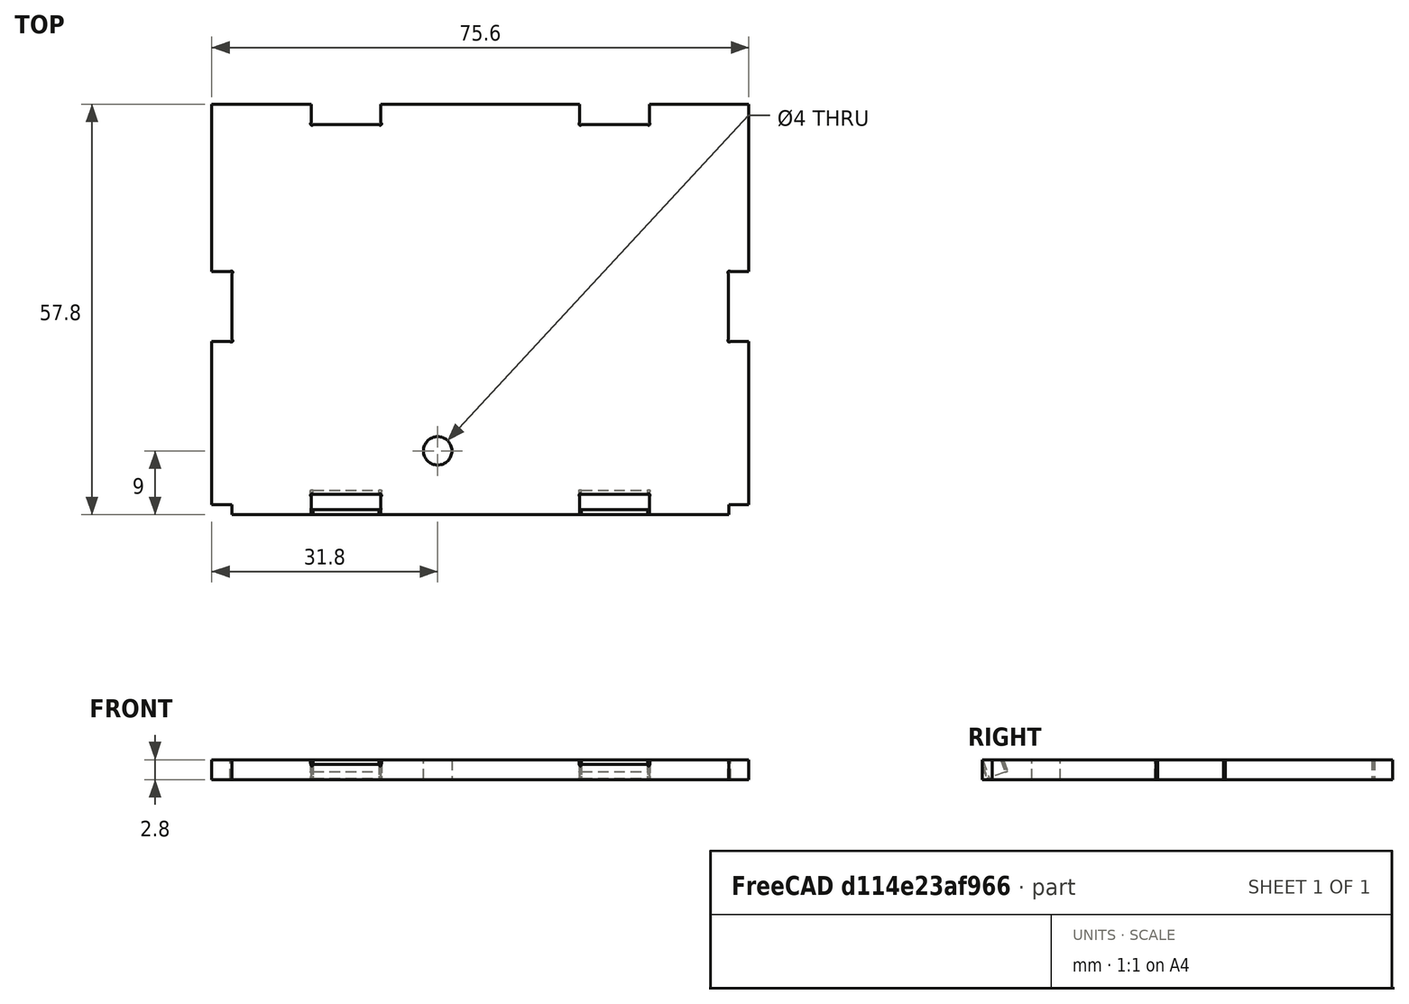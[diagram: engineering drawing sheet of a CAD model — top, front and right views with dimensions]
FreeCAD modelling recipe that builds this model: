
FCSTD DOCUMENT  (FreeCAD 1.0R39109 (Git))
Label: TheThing_v7_tabs_export
License: All rights reserved
LicenseURL: http://www.ohwr.org/attachments/2388/cern_ohl_v_1_2.txt
objects: Part::Feature×13, Part::Part2DObjectPython×12
note: 25 computed .brp shape members not serialized (recipe doc carries the construction recipe); baked Part::Feature solids carry a one-line shape summary decoded from their .brp

FEATURE [Part::Feature] test
  Placement = pos=(37.4,65.5,67.8) rot=(0,1,0;1.5708rad)
  shape: bbox 100.6 x 80.6 x 2.8 mm, 82 faces (baked)
FEATURE [Part::Feature] test001
  Placement = pos=(180.8,65.5,67.8) rot=(0,-1,0;1.5708rad)
  shape: bbox 100.6 x 80.6 x 2.8 mm, 70 faces (baked)
FEATURE [Part::Feature] test002
  Placement = pos=(187,118.5,93.2) rot=(0,-1,0;3.14159rad)
  shape: bbox 75.6 x 47.6 x 2.8 mm, 48 faces (baked)
FEATURE [Part::Feature] test003
  Placement = pos=(110,152.1,67.4) rot=(0,0,1;0rad)
  shape: bbox 75.6 x 77.8 x 2.8 mm, 42 faces (baked)
FEATURE [Part::Feature] test004
  Placement = pos=(109.4,62.1,33.2) rot=(0,-1,0;3.14159rad)
  shape: bbox 75.6 x 33.14 x 2.8 mm, 54 faces (baked)
FEATURE [Part::Feature] test005
  Placement = pos=(33,168.92,78.0359) rot=(-0.34202,0,0;2.79253rad)
  shape: bbox 75.6 x 17.92 x 2.8 mm, 18 faces (baked)
FEATURE [Part::Feature] test006
  Placement = pos=(33,156,12.7) rot=(1,0,0;1.5708rad)
  shape: bbox 75.6 x 104.4 x 2.8 mm, 110 faces (baked)
FEATURE [Part::Feature] test007
  Placement = pos=(110,209.68,-27.7) rot=(-1,0,0;1.5708rad)
  shape: bbox 75.6 x 44.36 x 2.8 mm, 108 faces (baked)
FEATURE [Part::Feature] test008
  Placement = pos=(187,149.16,4.32219) rot=(-0.939693,0,0;1.22173rad)
  shape: bbox 75.6 x 58.09 x 2.923 mm, 53 faces (baked)
FEATURE [Part::Feature] test009
  Placement = pos=(37.5,65.5,65.8) rot=(0,1,0;1.5708rad)
  shape: bbox 109.8 x 89.8 x 2.8 mm, 46 faces (baked)
FEATURE [Part::Feature] test010
  Placement = pos=(180.8,65.5,-3) rot=(0,1,0;4.71239rad)
  shape: bbox 109.8 x 89.8 x 2.8 mm, 46 faces (baked)
FEATURE [Part::Part2DObjectPython] Shape2DView  # Draft 2D object (typed FeaturePython)
  AutoUpdate = true
  Base = -> test
  Clip = false
  FuseArch = false
  HiddenLines = false
  InPlace = true
  OnlySolids = false
  Projection = (0,0,1)
  ProjectionMode = 0
  SegmentLength = 0.05
  Tessellation = false
  VisibleOnly = false
FEATURE [Part::Part2DObjectPython] Shape2DView001  # Draft 2D object (typed FeaturePython)
  AutoUpdate = true
  Base = -> test001
  Clip = false
  FuseArch = false
  HiddenLines = false
  InPlace = true
  OnlySolids = false
  Projection = (0,0,1)
  ProjectionMode = 0
  SegmentLength = 0.05
  Tessellation = false
  VisibleOnly = false
FEATURE [Part::Part2DObjectPython] Shape2DView002  # Draft 2D object (typed FeaturePython)
  AutoUpdate = true
  Base = -> test002
  Clip = false
  FuseArch = false
  HiddenLines = false
  InPlace = true
  OnlySolids = false
  Projection = (0,0,1)
  ProjectionMode = 0
  SegmentLength = 0.05
  Tessellation = false
  VisibleOnly = false
FEATURE [Part::Part2DObjectPython] Shape2DView003  # Draft 2D object (typed FeaturePython)
  AutoUpdate = true
  Base = -> test003
  Clip = false
  FuseArch = false
  HiddenLines = false
  InPlace = true
  OnlySolids = false
  Projection = (0,0,1)
  ProjectionMode = 0
  SegmentLength = 0.05
  Tessellation = false
  VisibleOnly = false
FEATURE [Part::Part2DObjectPython] Shape2DView004  # Draft 2D object (typed FeaturePython)
  AutoUpdate = true
  Base = -> test004
  Clip = false
  FuseArch = false
  HiddenLines = false
  InPlace = true
  OnlySolids = false
  Projection = (0,0,1)
  ProjectionMode = 0
  SegmentLength = 0.05
  Tessellation = false
  VisibleOnly = false
FEATURE [Part::Part2DObjectPython] Shape2DView005  # Draft 2D object (typed FeaturePython)
  AutoUpdate = true
  Base = -> test005
  Clip = false
  FuseArch = false
  HiddenLines = false
  InPlace = true
  OnlySolids = false
  Projection = (0,0,1)
  ProjectionMode = 0
  SegmentLength = 0.05
  Tessellation = false
  VisibleOnly = false
FEATURE [Part::Part2DObjectPython] Shape2DView006  # Draft 2D object (typed FeaturePython)
  AutoUpdate = true
  Base = -> test006
  Clip = false
  FuseArch = false
  HiddenLines = false
  InPlace = true
  OnlySolids = false
  Projection = (0,0,1)
  ProjectionMode = 0
  SegmentLength = 0.05
  Tessellation = false
  VisibleOnly = false
FEATURE [Part::Part2DObjectPython] Shape2DView007  # Draft 2D object (typed FeaturePython)
  AutoUpdate = true
  Base = -> test007
  Clip = false
  FuseArch = false
  HiddenLines = false
  InPlace = true
  OnlySolids = false
  Projection = (0,0,1)
  ProjectionMode = 0
  SegmentLength = 0.05
  Tessellation = false
  VisibleOnly = false
FEATURE [Part::Part2DObjectPython] Shape2DView009  # Draft 2D object (typed FeaturePython)
  AutoUpdate = true
  Base = -> test009
  Clip = false
  FuseArch = false
  HiddenLines = false
  InPlace = true
  OnlySolids = false
  Projection = (0,0,1)
  ProjectionMode = 0
  SegmentLength = 0.05
  Tessellation = false
  VisibleOnly = false
FEATURE [Part::Part2DObjectPython] Shape2DView010  # Draft 2D object (typed FeaturePython)
  AutoUpdate = true
  Base = -> test010
  Clip = false
  FuseArch = false
  HiddenLines = false
  InPlace = true
  OnlySolids = false
  Projection = (0,0,1)
  ProjectionMode = 0
  SegmentLength = 0.05
  Tessellation = false
  VisibleOnly = false
FEATURE [Part::Part2DObjectPython] Shape2DView008  # Draft 2D object (typed FeaturePython)
  AutoUpdate = true
  Base = -> test008
  Clip = false
  FuseArch = false
  HiddenLines = false
  InPlace = true
  OnlySolids = false
  Projection = (0,0,1)
  ProjectionMode = 0
  SegmentLength = 0.05
  Tessellation = false
  VisibleOnly = false
FEATURE [Part::Feature] test011
  Placement = pos=(272,149.16,4.32219) rot=(-0.939693,0,0;1.22173rad)
  shape: bbox 75.6 x 58.09 x 2.923 mm, 53 faces (baked)
FEATURE [Part::Feature] Face
  shape: bbox 75.6 x 57.8 x 2e-07 mm, 1 faces, 0 solids (baked)
FEATURE [Part::Part2DObjectPython] Shape2DView012  # Draft 2D object (typed FeaturePython)
  AutoUpdate = true
  Base = -> Face
  Clip = false
  FuseArch = false
  HiddenLines = false
  InPlace = true
  OnlySolids = false
  Placement = pos=(-85,0,0) rot=(0,0,1;0rad)
  Projection = (0,0,1)
  ProjectionMode = 0
  SegmentLength = 0.05
  Tessellation = false
  VisibleOnly = false
